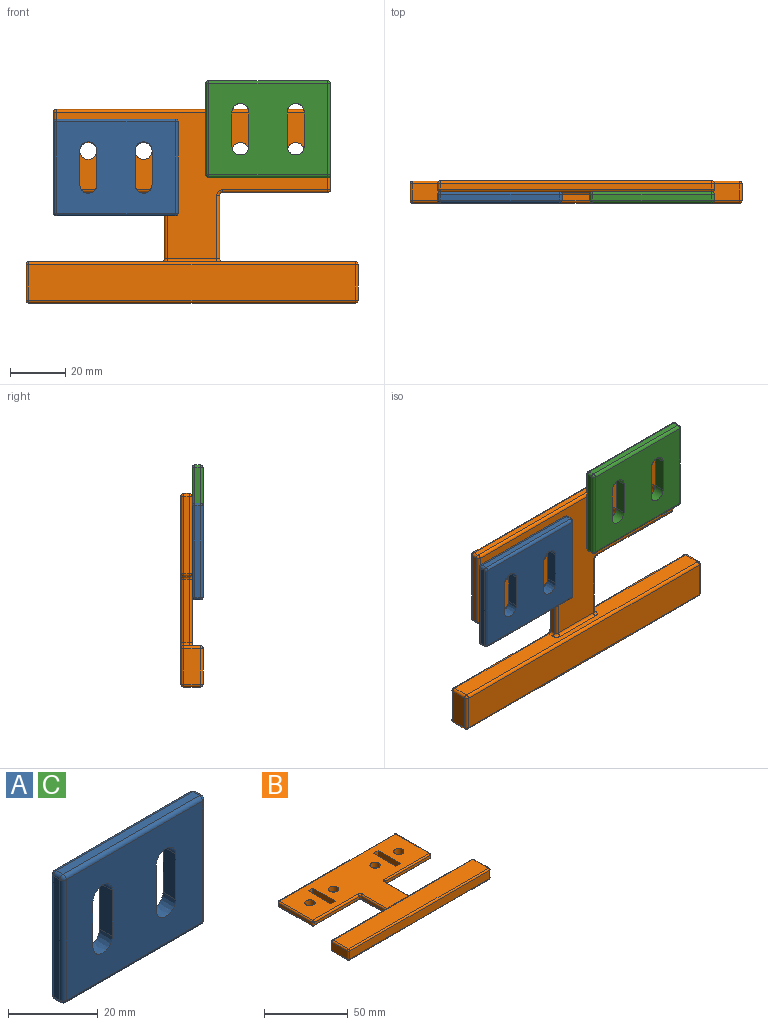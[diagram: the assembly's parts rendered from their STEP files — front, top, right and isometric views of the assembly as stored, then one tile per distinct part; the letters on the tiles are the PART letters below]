
ASSEMBLY  parts=3 mates=4
PART A: 43 faces, bbox 45x8x35 mm
  f0: plane 43x2mm, normal (0,0,-1), area 86mm2, adj f22,f27,f30,f33
  f1: plane 33x2mm, normal (1,0,0), area 66mm2, adj f19,f28,f29,f33
  f2: plane 43x2mm, normal (0,0,1), area 86mm2, adj f14,f18,f19,f20
  f3: plane 12.5x4mm, normal (1,0,0), area 50mm2, adj f4,f9,f12,f13
  f4: cylinder r=3.05mm len=6.1mm, axis (0,1,0), area 38.3mm2, adj f3,f5,f12,f13
  f5: plane 12.5x4mm, normal (-1,0,0), area 50mm2, adj f4,f9,f12,f13
  f6: extruded ~6.1x4mm, area 38.3mm2, adj f7,f10,f12,f13
  f7: plane 12.5x4mm, normal (1,0,0), area 50mm2, adj f6,f8,f12,f13
  f8: cylinder r=3.05mm len=6.1mm, axis (0,1,0), area 38.3mm2, adj f7,f10,f12,f13
  f9: extruded ~6.1x4mm, area 38.3mm2, adj f3,f5,f12,f13
  f10: plane 12.5x4mm, normal (-1,0,0), area 50mm2, adj f6,f8,f12,f13
  f11: plane 33x2mm, normal (-1,0,0), area 66mm2, adj f14,f17,f21,f22
  f12: plane 43x33mm, normal (0,-1,0), area 1208mm2, adj f3,f4,f5,f6,f7,f8,f9,f10
  f13: plane 43x33mm, normal (0,1,0), area 1189.5mm2, adj f3,f4,f5,f6,f7,f8,f9,f10
  f14: cylinder r=1mm len=2mm, axis (0,-1,0), area 3.1mm2, adj f2,f11,f15,f16
  f15: sphere r=1mm, area 1.6mm2, adj f14,f17,f18
  f16: sphere r=1mm, area 1.6mm2, adj f14,f20,f21
  f17: cylinder r=1mm len=33mm, axis (0,0,1), area 51.8mm2, adj f11,f12,f15,f23
  f18: cylinder r=1mm len=43mm, axis (1,0,0), area 67.5mm2, adj f2,f12,f15,f24
  f19: cylinder r=1mm len=2mm, axis (0,1,0), area 3.1mm2, adj f1,f2,f24,f25
  f20: cylinder r=1mm len=43mm, axis (-1,0,0), area 67.5mm2, adj f2,f13,f16,f25
  f21: cylinder r=1mm len=33mm, axis (0,0,-1), area 51.8mm2, adj f11,f13,f16,f26
  f22: cylinder r=1mm len=2mm, axis (0,1,0), area 3.1mm2, adj f0,f11,f23,f26
  f23: sphere r=1mm, area 1.6mm2, adj f17,f22,f27
  f24: sphere r=1mm, area 1.6mm2, adj f18,f19,f28
  f25: sphere r=1mm, area 1.6mm2, adj f19,f20,f29
  f26: sphere r=1mm, area 1.6mm2, adj f21,f22,f30
  f27: cylinder r=1mm len=43mm, axis (-1,0,0), area 67.5mm2, adj f0,f12,f23,f31
  f28: cylinder r=1mm len=33mm, axis (0,0,-1), area 51.8mm2, adj f1,f12,f24,f31
  f29: cylinder r=1mm len=33mm, axis (0,0,1), area 51.8mm2, adj f1,f13,f25,f32
  f30: cylinder r=1mm len=43mm, axis (1,0,0), area 67.5mm2, adj f0,f13,f26,f32
  f31: sphere r=1mm, area 1.6mm2, adj f27,f28,f33
  f32: sphere r=1mm, area 1.6mm2, adj f29,f30,f33
  f33: cylinder r=1mm len=2mm, axis (0,-1,0), area 3.1mm2, adj f0,f1,f31,f32
  f34: plane 3.75x3.7mm, normal (0,0,1), area 13.9mm2, adj f13,f35,f37,f39
  f35: plane 5x3.75mm, normal (1,0,0), area 18.8mm2, adj f13,f34,f36,f40
  f36: plane 3.75x3.7mm, normal (0,0,-1), area 13.9mm2, adj f13,f35,f37,f42
  f37: plane 5x3.75mm, normal (-1,0,0), area 18.8mm2, adj f13,f34,f36,f41
  f38: plane 4.5x3.2mm, normal (0,1,0), area 14.4mm2, adj f39,f40,f41,f42
  f39: cylinder r=0.25mm len=3.7mm, axis (-1,0,0), area 1.4mm2, adj f34,f38,f40,f41
  f40: cylinder r=0.25mm len=5mm, axis (0,0,1), area 1.9mm2, adj f35,f38,f39,f42
  f41: cylinder r=0.25mm len=5mm, axis (0,0,-1), area 1.9mm2, adj f37,f38,f39,f42
  f42: cylinder r=0.25mm len=3.7mm, axis (1,0,0), area 1.4mm2, adj f36,f38,f40,f41
PART B: 86 faces, bbox 120x70x8 mm
  f0: plane 98x53mm, normal (0,0,1), area 2930.6mm2, adj f8,f9,f10,f12,f22,f23,f32,f33
  f1: plane 118x68mm, normal (0,0,-1), area 4502.3mm2, adj f8,f9,f10,f12,f20,f25,f29,f30
  f2: plane 38x2mm, normal (0,-1,0), area 76mm2, adj f44,f45,f59,f60
  f3: plane 23x2mm, normal (-1,0,0), area 46mm2, adj f60,f61,f71,f72
  f4: plane 23x2mm, normal (1,0,0), area 46mm2, adj f34,f35,f46,f47
  f5: plane 38x2mm, normal (0,-1,0), area 76mm2, adj f24,f25,f33,f34
  f6: plane 28x2mm, normal (1,0,0), area 56mm2, adj f20,f21,f23,f24
  f7: plane 98x2mm, normal (0,1,0), area 196mm2, adj f21,f22,f30,f31
  f8: cylinder r=3.05mm len=6.1mm, axis (0,0,-1), area 76.7mm2, adj f0,f1
  f9: cylinder r=3.05mm len=6.1mm, axis (0,0,-1), area 76.7mm2, adj f0,f1
  f10: cylinder r=3.05mm len=6.1mm, axis (0,0,-1), area 76.7mm2, adj f0,f1
  f11: plane 28x2mm, normal (-1,0,0), area 56mm2, adj f31,f32,f43,f44
  f12: cylinder r=3.05mm len=6.1mm, axis (0,0,-1), area 76.7mm2, adj f0,f1
  f13: plane 118x6mm, normal (0,1,0), area 621.7mm2, adj f36,f47,f48,f55,f62,f63,f68,f72
  f14: plane 13x6mm, normal (-1,0,0), area 78mm2, adj f64,f65,f73,f74
  f15: plane 118x6mm, normal (0,-1,0), area 708mm2, adj f50,f51,f65,f66
  f16: plane 13x6mm, normal (1,0,0), area 78mm2, adj f48,f49,f51,f52
  f17: plane 118x13mm, normal (0,0,1), area 1534mm2, adj f49,f50,f63,f64
  f18: sphere r=1mm, area 1.6mm2, adj f21,f22,f23
  f19: sphere r=1mm, area 1.6mm2, adj f20,f24,f25
  f20: cylinder r=1mm len=28mm, axis (0,1,0), area 44mm2, adj f1,f6,f19,f26
  f21: cylinder r=1mm len=2mm, axis (0,0,-1), area 3.1mm2, adj f6,f7,f18,f26
  f22: cylinder r=1mm len=98mm, axis (1,0,0), area 153.9mm2, adj f0,f7,f18,f27
  f23: cylinder r=1mm len=28mm, axis (0,-1,0), area 44mm2, adj f0,f6,f18,f28
  f24: cylinder r=1mm len=2mm, axis (0,0,1), area 3.1mm2, adj f5,f6,f19,f28
  f25: cylinder r=1mm len=38mm, axis (1,0,0), area 59.7mm2, adj f1,f5,f19,f29
  f26: sphere r=1mm, area 1.6mm2, adj f20,f21,f30
  f27: sphere r=1mm, area 1.6mm2, adj f22,f31,f32
  f28: sphere r=1mm, area 1.6mm2, adj f23,f24,f33
  f29: torus R=2mm, axis (0,0,1), area 3.4mm2, adj f1,f25,f34,f35
  f30: cylinder r=1mm len=98mm, axis (-1,0,0), area 153.9mm2, adj f1,f7,f26,f37
  f31: cylinder r=1mm len=2mm, axis (0,0,1), area 3.1mm2, adj f7,f11,f27,f37
  f32: cylinder r=1mm len=28mm, axis (0,1,0), area 44mm2, adj f0,f11,f27,f38
  f33: cylinder r=1mm len=38mm, axis (-1,0,0), area 59.7mm2, adj f0,f5,f28,f39
  f34: cylinder r=1mm len=2mm, axis (0,0,-1), area 3.1mm2, adj f4,f5,f29,f39
  f35: cylinder r=1mm len=23mm, axis (0,1,0), area 36.1mm2, adj f1,f4,f29,f41
  f36: cylinder r=1mm len=48mm, axis (-1,0,0), area 75.4mm2, adj f1,f13,f41,f42
  f37: sphere r=1mm, area 1.6mm2, adj f30,f31,f43
  f38: sphere r=1mm, area 1.6mm2, adj f32,f44,f45
  f39: torus R=2mm, axis (0,0,1), area 3.4mm2, adj f0,f33,f34,f46
  f40: sphere r=1mm, area 1.6mm2, adj f49,f50,f51
  f41: torus R=2mm, axis (0,0,1), area 3.4mm2, adj f1,f35,f36,f47
  f42: sphere r=1mm, area 1.6mm2, adj f36,f48,f52
  f43: cylinder r=1mm len=28mm, axis (0,-1,0), area 44mm2, adj f1,f11,f37,f53
  f44: cylinder r=1mm len=2mm, axis (0,0,-1), area 3.1mm2, adj f2,f11,f38,f53
  f45: cylinder r=1mm len=38mm, axis (-1,0,0), area 59.7mm2, adj f0,f2,f38,f54
  f46: cylinder r=1mm len=23mm, axis (0,-1,0), area 36.1mm2, adj f0,f4,f39,f55
  f47: cylinder r=1mm len=2mm, axis (0,0,1), area 3.1mm2, adj f4,f13,f41,f55
  f48: cylinder r=1mm len=6mm, axis (0,0,-1), area 9.4mm2, adj f13,f16,f42,f56
  f49: cylinder r=1mm len=13mm, axis (0,-1,0), area 20.4mm2, adj f16,f17,f40,f56
  f50: cylinder r=1mm len=118mm, axis (-1,0,0), area 185.4mm2, adj f15,f17,f40,f57
  f51: cylinder r=1mm len=6mm, axis (0,0,1), area 9.4mm2, adj f15,f16,f40,f58
  f52: cylinder r=1mm len=13mm, axis (0,1,0), area 20.4mm2, adj f1,f16,f42,f58
  f53: sphere r=1mm, area 1.6mm2, adj f43,f44,f59
  f54: torus R=2mm, axis (0,0,1), area 3.4mm2, adj f0,f45,f60,f61
  f55: torus R=2mm, axis (0,-1,0), area 3.4mm2, adj f13,f46,f47,f62
  f56: sphere r=1mm, area 1.6mm2, adj f48,f49,f63
  f57: sphere r=1mm, area 1.6mm2, adj f50,f64,f65
  f58: sphere r=1mm, area 1.6mm2, adj f51,f52,f66
  f59: cylinder r=1mm len=38mm, axis (1,0,0), area 59.7mm2, adj f1,f2,f53,f67
  f60: cylinder r=1mm len=2mm, axis (0,0,1), area 3.1mm2, adj f2,f3,f54,f67
  f61: cylinder r=1mm len=23mm, axis (0,1,0), area 36.1mm2, adj f0,f3,f54,f68
  f62: cylinder r=1mm len=18mm, axis (-1,0,0), area 28.3mm2, adj f0,f13,f55,f68
  f63: cylinder r=1mm len=118mm, axis (1,0,0), area 185.4mm2, adj f13,f17,f56,f69
  f64: cylinder r=1mm len=13mm, axis (0,1,0), area 20.4mm2, adj f14,f17,f57,f69
  f65: cylinder r=1mm len=6mm, axis (0,0,-1), area 9.4mm2, adj f14,f15,f57,f70
  f66: cylinder r=1mm len=118mm, axis (1,0,0), area 185.4mm2, adj f1,f15,f58,f70
  f67: torus R=2mm, axis (0,0,1), area 3.4mm2, adj f1,f59,f60,f71
  f68: torus R=2mm, axis (0,-1,0), area 3.4mm2, adj f13,f61,f62,f72
  f69: sphere r=1mm, area 1.6mm2, adj f63,f64,f73
  f70: sphere r=1mm, area 1.6mm2, adj f65,f66,f74
  f71: cylinder r=1mm len=23mm, axis (0,-1,0), area 36.1mm2, adj f1,f3,f67,f75
  f72: cylinder r=1mm len=2mm, axis (0,0,-1), area 3.1mm2, adj f3,f13,f68,f75
  f73: cylinder r=1mm len=6mm, axis (0,0,1), area 9.4mm2, adj f13,f14,f69,f76
  f74: cylinder r=1mm len=13mm, axis (0,-1,0), area 20.4mm2, adj f1,f14,f70,f76
  f75: torus R=2mm, axis (0,0,1), area 3.4mm2, adj f1,f71,f72,f77
  f76: sphere r=1mm, area 1.6mm2, adj f73,f74,f77
  f77: cylinder r=1mm len=48mm, axis (-1,0,0), area 75.4mm2, adj f1,f13,f75,f76
  f78: plane 4x3.9mm, normal (0,-1,0), area 15.6mm2, adj f0,f1,f79,f81
  f79: plane 19x4mm, normal (1,0,0), area 76mm2, adj f0,f1,f78,f80
  f80: plane 4x3.9mm, normal (0,1,0), area 15.6mm2, adj f0,f1,f79,f81
  f81: plane 19x4mm, normal (-1,0,0), area 76mm2, adj f0,f1,f78,f80
  f82: plane 4x3.9mm, normal (0,-1,0), area 15.6mm2, adj f0,f1,f83,f85
  f83: plane 19x4mm, normal (1,0,0), area 76mm2, adj f0,f1,f82,f84
  f84: plane 4x3.9mm, normal (0,1,0), area 15.6mm2, adj f0,f1,f83,f85
  f85: plane 19x4mm, normal (-1,0,0), area 76mm2, adj f0,f1,f82,f84
PART C: same geometry as A
PLACE A rot(axis=(0,-1,0),0deg) t=(-5,0,31.52)mm
PLACE B rot(axis=(1,0,0),90deg) t=(60,4,0)mm
PLACE C rot(axis=(0,-1,0),180deg) t=(5,0,80.35)mm
MATE planar C.f13 <-> B.f9  axis (0,1,0) through (37.5,0,72.15)mm
MATE planar C.f11 <-> B.f6  axis (1,0,0) through (50,-2,62.85)mm
MATE planar A.f13 <-> B.f0  axis (0,1,0) through (-27.5,0,49.02)mm
MATE planar A.f11 <-> B.f11  axis (-1,0,0) through (-50,-2,49.02)mm
